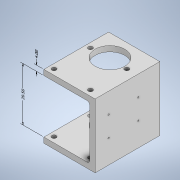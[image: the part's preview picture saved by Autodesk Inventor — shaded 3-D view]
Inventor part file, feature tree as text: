
AUTODESK INVENTOR PART (.ipt)
format: ipt  version: 2022 (Build 260153000, 153)  size: 185,856 bytes
history: native  units: mm
features: sketch x5, other x3, hole x3, extrude x2, fillet x1
ambient origin geometry x8: Origin, YZ Plane, XZ Plane, XY Plane, X Axis, Y Axis, Z Axis, Center Point
bodies: Body1 (feature_tree)
feature tree (14):
  other  "ソリッド1"
  extrude  "押し出し1"  Depth=48.0mm
  extrude  "押し出し2"  Depth=38.0mm
  hole  "穴1"  [1 undecoded]
  hole  "穴2"  [1 undecoded]
  hole  "穴4"  [1 undecoded]
  fillet  "フィレット1"  Radius=4.0mm
  sketch  "スケッチ1"
  sketch  "スケッチ2"
  sketch  "スケッチ3"
  sketch  "スケッチ4"
  sketch  "スケッチ6"
  other  "長さ寸法 1"
  other  "長さ寸法 2"
note: 3 required parameter values undecoded (feature->parameter linkage not recoverable at this tier; creation-order binding heuristic only, values carry confidence <= 0.55)
